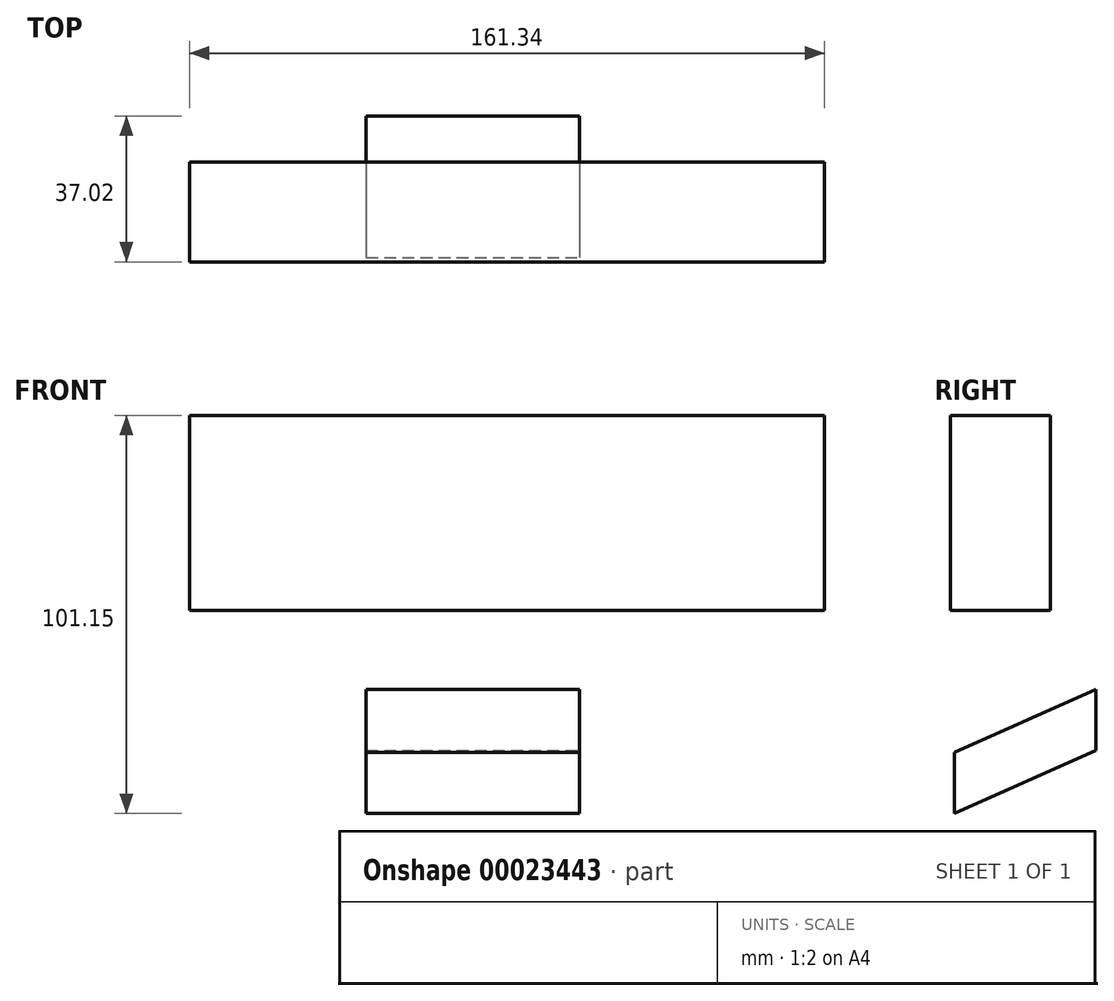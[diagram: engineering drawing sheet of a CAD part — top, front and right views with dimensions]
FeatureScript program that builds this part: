
annotation { "Feature Type Name" : "Feature", "Feature Type Description" : "" }
export const myFeature = defineFeature(function(context is Context, id is Id, definition is map)
    precondition{}
    {
        {
            var Q0;
            Q0=qCreatedBy(makeId("Front.planeOp"),FACE);
            var sketch = newSketch(context, id + "F0", { "sketchPlane" : qUnion([Q0])});
            skLineSegment(sketch, "E0.bottom", {"start": v(-53.68, 24.75) * mm, "end": v(107.66, 24.75) * mm});
            skLineSegment(sketch, "E0.top", {"start": v(-53.68, -24.88) * mm, "end": v(107.66, -24.88) * mm});
            skLineSegment(sketch, "E0.left", {"start": v(-53.68, 24.75) * mm, "end": v(-53.68, -24.88) * mm});
            skLineSegment(sketch, "E0.right", {"start": v(107.66, 24.75) * mm, "end": v(107.66, -24.88) * mm});
            skSolve(sketch);
        }
        {
            var Q0;
            Q0=makeQuery(id+"F0.imprint","IMPRINT",FACE,{"disambiguationData":[TD([[makeQuery(id+"F0.imprint","IMPRINT",EDGE,{"derivedFrom":sQuery(id+"F0.wireOp",EDGE,"E0.bottom")}),-1.0]])]});
            extrude(context, id + "F1", {"entities" : qUnion([Q0]), "depth" : 25.4 * mm});
        }
        {
            var Q0;
            Q0=qCreatedBy(makeId("Right.planeOp"),FACE);
            var sketch = newSketch(context, id + "F2", { "sketchPlane" : qUnion([Q0])});
            skLineSegment(sketch, "E1", {"start": v(-24.33, -69.1) * mm, "end": v(11.62, -53.02) * mm});
            skSolve(sketch);
        }
        {
            var Q0;
            Q0=qCreatedBy(makeId("Front.planeOp"),FACE);
            var sketch = newSketch(context, id + "F3", { "sketchPlane" : qUnion([Q0])});
            skLineSegment(sketch, "E2.bottom", {"start": v(-8.75, -65.52) * mm, "end": v(45.48, -65.52) * mm});
            skLineSegment(sketch, "E2.top", {"start": v(-8.75, -50.03) * mm, "end": v(45.48, -50.03) * mm});
            skLineSegment(sketch, "E2.left", {"start": v(-8.75, -65.52) * mm, "end": v(-8.75, -50.03) * mm});
            skLineSegment(sketch, "E2.right", {"start": v(45.48, -65.52) * mm, "end": v(45.48, -50.03) * mm});
            skSolve(sketch);
        }
        {
            var Q0;
            Q0=makeQuery(id+"F3.imprint","IMPRINT",FACE,{"disambiguationData":[TD([[makeQuery(id+"F3.imprint","IMPRINT",EDGE,{"derivedFrom":sQuery(id+"F3.wireOp",EDGE,"E2.bottom")}),1.0]])]});
            var Q1;
            Q1=sQuery(id+"F2.wireOp",EDGE,"E1");
            sweep(context, id + "F4", {"profiles" : qUnion([Q0]), "path" : qUnion([Q1])});
        }
    });
